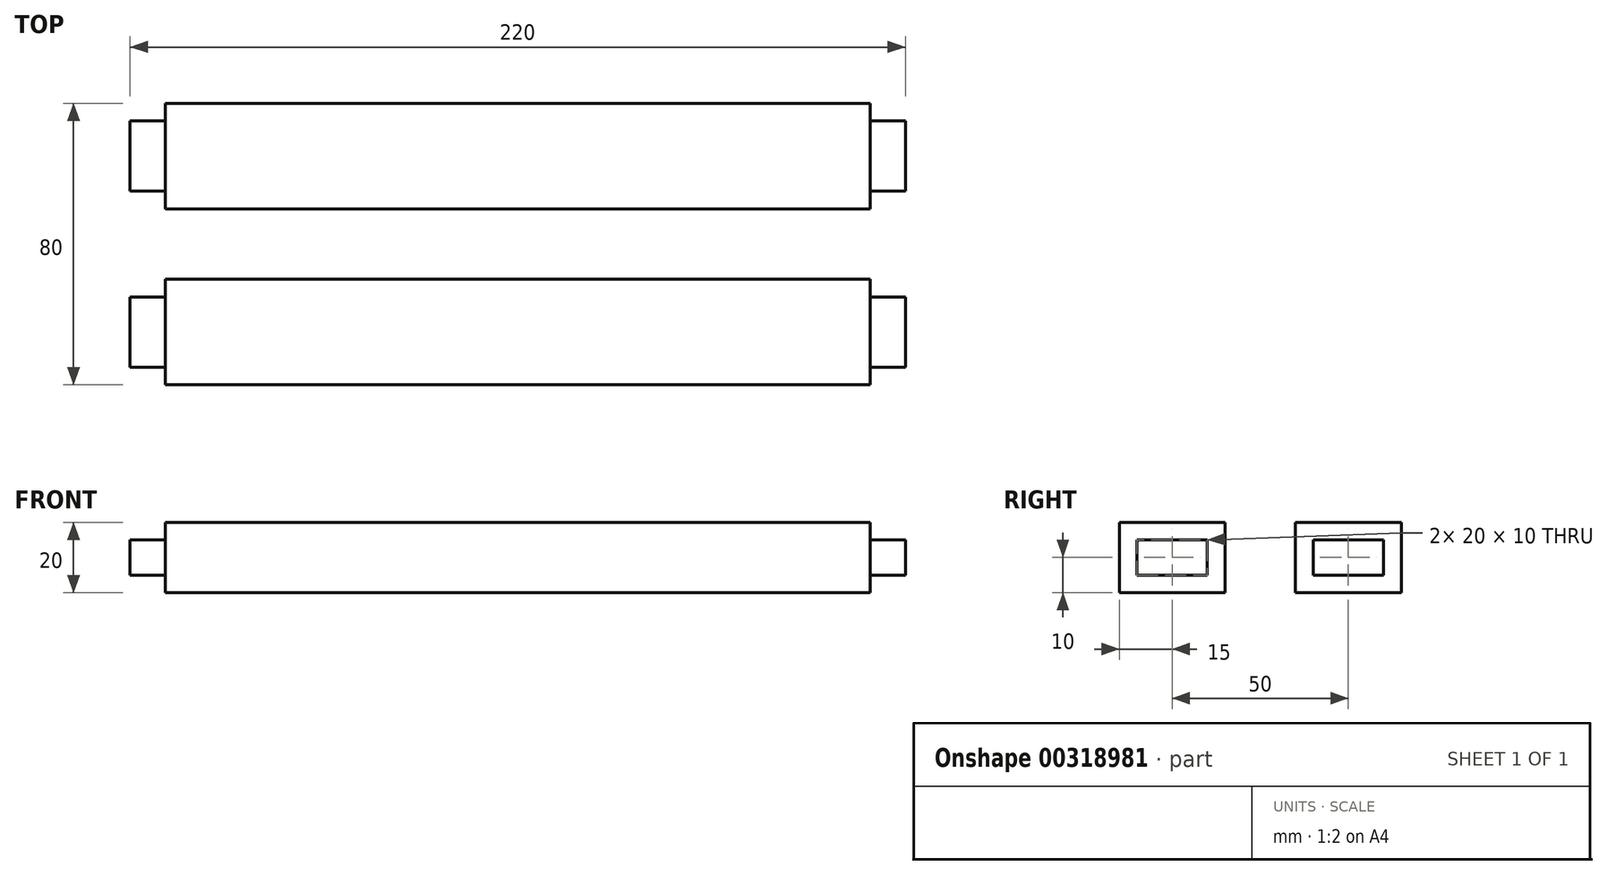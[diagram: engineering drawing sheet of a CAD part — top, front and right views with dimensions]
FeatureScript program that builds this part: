
annotation { "Feature Type Name" : "Feature", "Feature Type Description" : "" }
export const myFeature = defineFeature(function(context is Context, id is Id, definition is map)
    precondition{}
    {
        {
            var Q0;
            Q0=qCreatedBy(makeId("Top.planeOp"),FACE);
            var sketch = newSketch(context, id + "F0", { "sketchPlane" : qUnion([Q0])});
            skLineSegment(sketch, "E0.bottom", {"start": v(100, 15) * mm, "end": v(-100, 15) * mm});
            skLineSegment(sketch, "E0.top", {"start": v(100, -15) * mm, "end": v(-100, -15) * mm});
            skLineSegment(sketch, "E0.left", {"start": v(100, 15) * mm, "end": v(100, -15) * mm});
            skLineSegment(sketch, "E0.right", {"start": v(-100, 15) * mm, "end": v(-100, -15) * mm});
            skPoint(sketch, "E0.middle", {"position": v(0, 0) * mm});
            skSolve(sketch);
        }
        {
            var Q0;
            Q0 = qSketchRegion(id + "F0", true);
            extrude(context, id + "F1", {"entities" : qUnion([Q0]), "depth" : 20 * mm});
        }
        {
            var Q0;
            Q0=makeQuery(id+"F1.opExtrude","SWEPT_FACE",FACE,{"disambiguationData":[OSD([sQuery(id+"F0.wireOp",EDGE,"E0.left")])]});
            var sketch = newSketch(context, id + "F2", { "sketchPlane" : qUnion([Q0])});
            skLineSegment(sketch, "E1", {"start": v(-15, 15) * mm, "end": v(-10, 15) * mm, "construction": true});
            skLineSegment(sketch, "E2", {"start": v(-10, 15) * mm, "end": v(-10, 20) * mm, "construction": true});
            skLineSegment(sketch, "E3.bottom", {"start": v(-10, 15) * mm, "end": v(10, 15) * mm});
            skLineSegment(sketch, "E3.top", {"start": v(-10, 5) * mm, "end": v(10, 5) * mm});
            skLineSegment(sketch, "E3.left", {"start": v(-10, 15) * mm, "end": v(-10, 5) * mm});
            skLineSegment(sketch, "E3.right", {"start": v(10, 15) * mm, "end": v(10, 5) * mm});
            skSolve(sketch);
        }
        {
            var Q0;
            Q0 = qSketchRegion(id + "F2", true);
            extrude(context, id + "F3", {"entities" : qUnion([Q0]), "operationType" : NewBodyOperationType.ADD, "depth" : 10 * mm});
        }
        {
            var Q0;
            Q0=makeQuery(id+"F1.opExtrude","SWEPT_BODY",BODY,{"disambiguationData":[OSD([sQuery(id+"F0.wireOp",EDGE,"E0.bottom"),sQuery(id+"F0.wireOp",EDGE,"E0.top"),sQuery(id+"F0.wireOp",EDGE,"E0.left"),sQuery(id+"F0.wireOp",EDGE,"E0.right")])]});
            var Q1;
            Q1=qCreatedBy(makeId("Right.planeOp"),FACE);
            mirror(context, id + "F4", {"operationType" : NewBodyOperationType.ADD, "entities" : qUnion([Q0]), "mirrorPlane" : qUnion([Q1])});
        }
        {
            var Q0;
            Q0=makeQuery(id+"F1.opExtrude","SWEPT_BODY",BODY,{"disambiguationData":[OSD([sQuery(id+"F0.wireOp",EDGE,"E0.bottom"),sQuery(id+"F0.wireOp",EDGE,"E0.top"),sQuery(id+"F0.wireOp",EDGE,"E0.left"),sQuery(id+"F0.wireOp",EDGE,"E0.right")])]});
            transform(context, id + "F5", {"entities" : qUnion([Q0]), "transformType" : TransformType.TRANSLATION_3D, "dx" : 0 * mm, "dy" : 50 * mm, "dz" : 0 * mm, "makeCopy" : true});
        }
    });
